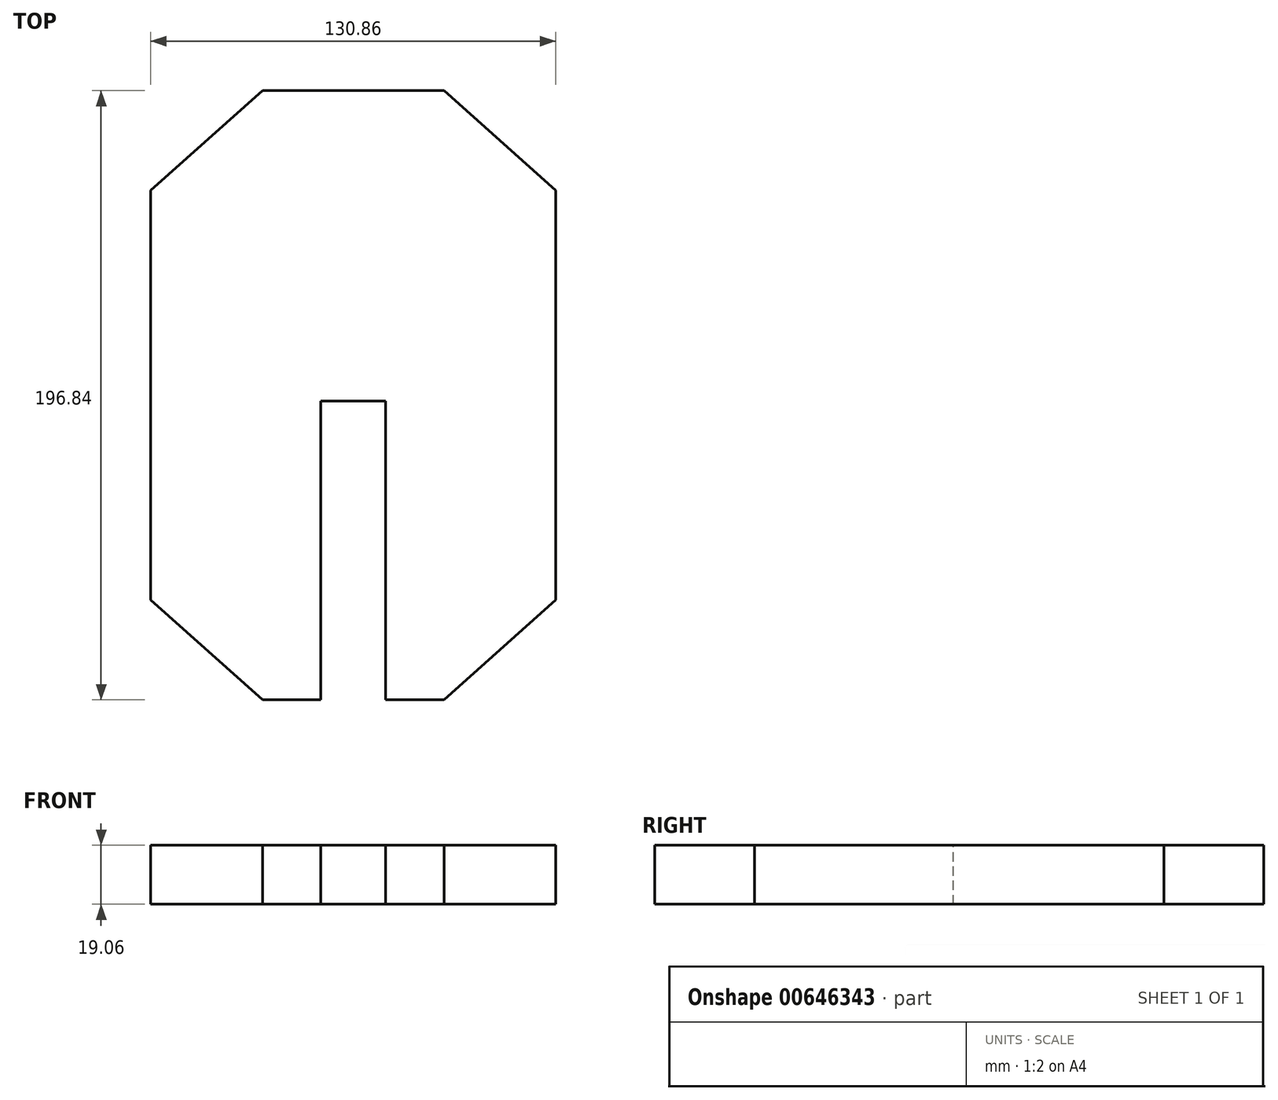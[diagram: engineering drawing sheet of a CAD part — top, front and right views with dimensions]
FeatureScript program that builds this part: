
annotation { "Feature Type Name" : "Feature", "Feature Type Description" : "" }
export const myFeature = defineFeature(function(context is Context, id is Id, definition is map)
    precondition{}
    {
        {
            var Q0;
            Q0=qCreatedBy(makeId("Top.planeOp"),FACE);
            var sketch = newSketch(context, id + "F0", { "sketchPlane" : qUnion([Q0])});
            skLineSegment(sketch, "E0.bottom", {"start": v(29.34, 98.42) * mm, "end": v(-29.34, 98.42) * mm});
            skLineSegment(sketch, "E0.top", {"start": v(29.34, -98.42) * mm, "end": v(-29.34, -98.42) * mm});
            skLineSegment(sketch, "E0.left", {"start": v(29.34, 98.42) * mm, "end": v(29.34, -98.42) * mm});
            skLineSegment(sketch, "E0.right", {"start": v(-29.34, 98.42) * mm, "end": v(-29.34, -98.42) * mm});
            skPoint(sketch, "E0.middle", {"position": v(0, 0) * mm});
            skLineSegment(sketch, "E1.bottom", {"start": v(-65.43, 66.17) * mm, "end": v(65.43, 66.17) * mm});
            skLineSegment(sketch, "E1.top", {"start": v(-65.43, -66.17) * mm, "end": v(65.43, -66.17) * mm});
            skLineSegment(sketch, "E1.left", {"start": v(-65.43, 66.17) * mm, "end": v(-65.43, -66.17) * mm});
            skLineSegment(sketch, "E1.right", {"start": v(65.43, 66.17) * mm, "end": v(65.43, -66.17) * mm});
            skLineSegment(sketch, "E2", {"start": v(-29.34, -98.42) * mm, "end": v(-65.43, -66.17) * mm});
            skLineSegment(sketch, "E3", {"start": v(29.34, -98.42) * mm, "end": v(65.43, -66.17) * mm});
            skLineSegment(sketch, "E4", {"start": v(65.43, 66.17) * mm, "end": v(29.34, 98.42) * mm});
            skLineSegment(sketch, "E5", {"start": v(-65.43, 66.17) * mm, "end": v(-29.34, 98.42) * mm});
            skSolve(sketch);
        }
        {
            var Q0;
            {var subQ0=sQuery(id+"F0.wireOp",EDGE,"E0.bottom");Q0=makeQuery(id+"F0.imprint","IMPRINT",FACE,{"disambiguationData":[TD([[makeQuery(id+"F0.imprint","IMPRINT",EDGE,{"derivedFrom":subQ0}),1.0]])]});}
            var Q1;
            {var subQ5=sQuery(id+"F0.wireOp",EDGE,"E1.left");Q1=makeQuery(id+"F0.imprint","IMPRINT",FACE,{"disambiguationData":[TD([[makeQuery(id+"F0.imprint","IMPRINT",EDGE,{"derivedFrom":subQ5}),1.0]])]});}
            var Q2;
            {var subQ0=sQuery(id+"F0.wireOp",EDGE,"E5");Q2=makeQuery(id+"F0.imprint","IMPRINT",FACE,{"disambiguationData":[TD([[makeQuery(id+"F0.imprint","IMPRINT",EDGE,{"derivedFrom":subQ0}),-1.0]])]});}
            var Q3;
            {var subQ0=sQuery(id+"F0.wireOp",EDGE,"E1.bottom");var subQ1=sQuery(id+"F0.wireOp",EDGE,"E0.left");var subQ2=makeQuery(id+"F0.imprint","INTERSECT",VERTEX,{"derivedFrom":[subQ1,subQ0]});Q3=makeQuery(id+"F0.imprint","IMPRINT",FACE,{"disambiguationData":[TD([[makeQuery(id+"F0.imprint","IMPRINT",EDGE,{"disambiguationData":[TD([[subQ2,-1.0]])],"derivedFrom":subQ1}),-1.0]])]});}
            var Q4;
            {var subQ5=sQuery(id+"F0.wireOp",EDGE,"E1.right");Q4=makeQuery(id+"F0.imprint","IMPRINT",FACE,{"disambiguationData":[TD([[makeQuery(id+"F0.imprint","IMPRINT",EDGE,{"derivedFrom":subQ5}),-1.0]])]});}
            var Q5;
            {var subQ0=sQuery(id+"F0.wireOp",EDGE,"E4");Q5=makeQuery(id+"F0.imprint","IMPRINT",FACE,{"disambiguationData":[TD([[makeQuery(id+"F0.imprint","IMPRINT",EDGE,{"derivedFrom":subQ0}),1.0]])]});}
            var Q6;
            {var subQ0=sQuery(id+"F0.wireOp",EDGE,"E3");Q6=makeQuery(id+"F0.imprint","IMPRINT",FACE,{"disambiguationData":[TD([[makeQuery(id+"F0.imprint","IMPRINT",EDGE,{"derivedFrom":subQ0}),1.0]])]});}
            var Q7;
            {var subQ0=sQuery(id+"F0.wireOp",EDGE,"E0.top");Q7=makeQuery(id+"F0.imprint","IMPRINT",FACE,{"disambiguationData":[TD([[makeQuery(id+"F0.imprint","IMPRINT",EDGE,{"derivedFrom":subQ0}),-1.0]])]});}
            var Q8;
            {var subQ0=sQuery(id+"F0.wireOp",EDGE,"E2");Q8=makeQuery(id+"F0.imprint","IMPRINT",FACE,{"disambiguationData":[TD([[makeQuery(id+"F0.imprint","IMPRINT",EDGE,{"derivedFrom":subQ0}),-1.0]])]});}
            extrude(context, id + "F1", {"entities" : qUnion([Q0, Q1, Q2, Q3, Q4, Q5, Q6, Q7, Q8]), "endBound" : BoundingType.SYMMETRIC, "depth" : 19.05 * mm, "offsetDistance" : 25.4 * mm});
        }
        {
            var Q0;
            Q0=qCreatedBy(makeId("Top.planeOp"),FACE);
            var sketch = newSketch(context, id + "F2", { "sketchPlane" : qUnion([Q0])});
            skLineSegment(sketch, "E6", {"start": v(-10.48, -98.42) * mm, "end": v(10.48, -98.42) * mm});
            skLineSegment(sketch, "E7", {"start": v(-10.48, -98.42) * mm, "end": v(-10.48, -1.9) * mm});
            skLineSegment(sketch, "E8", {"start": v(-10.48, -1.9) * mm, "end": v(10.48, -1.9) * mm});
            skLineSegment(sketch, "E9", {"start": v(10.48, -1.9) * mm, "end": v(10.48, -98.42) * mm});
            skSolve(sketch);
        }
        {
            var Q0;
            Q0 = qSketchRegion(id + "F2", true);
            extrude(context, id + "F3", {"entities" : qUnion([Q0]), "operationType" : NewBodyOperationType.REMOVE, "endBound" : BoundingType.SYMMETRIC, "oppositeDirection" : true, "depth" : 19.05 * mm, "offsetDistance" : 25.4 * mm});
        }
    });
